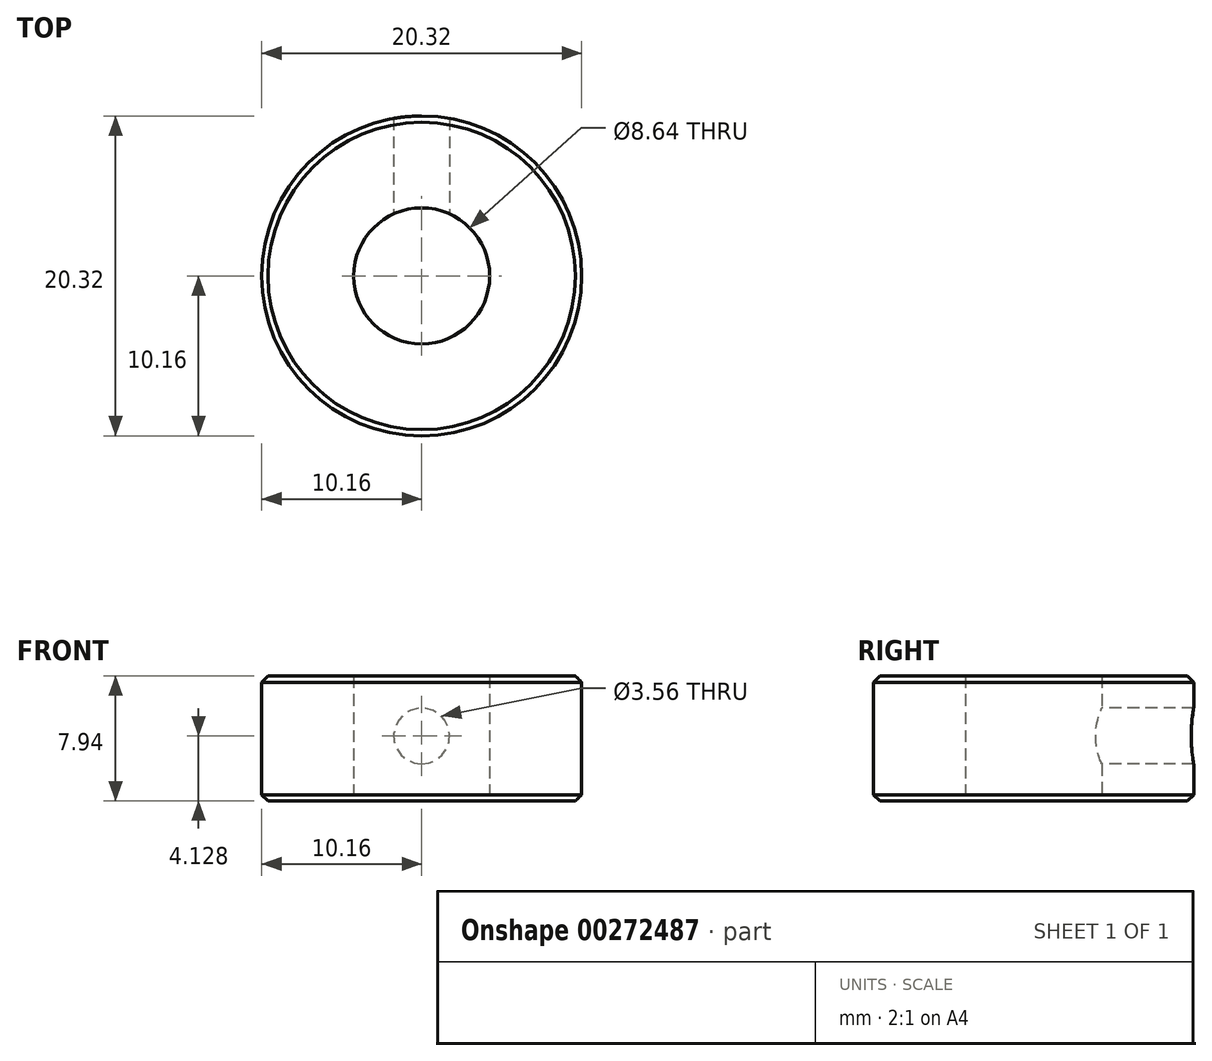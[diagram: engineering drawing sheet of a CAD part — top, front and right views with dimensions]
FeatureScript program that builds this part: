
annotation { "Feature Type Name" : "Feature", "Feature Type Description" : "" }
export const myFeature = defineFeature(function(context is Context, id is Id, definition is map)
    precondition{}
    {
        {
            var Q0;
            Q0=qCreatedBy(makeId("Top.planeOp"),FACE);
            var sketch = newSketch(context, id + "F0", { "sketchPlane" : qUnion([Q0])});
            skCircle(sketch, "E0", {"center": v(0, 0) * mm, "radius": 10.16 * mm});
            skCircle(sketch, "E1", {"center": v(0, 0) * mm, "radius": 4.32 * mm});
            skSolve(sketch);
        }
        {
            var Q0;
            Q0 = qSketchRegion(id + "F0", true);
            extrude(context, id + "F1", {"entities" : qUnion([Q0]), "depth" : 7.94 * mm});
        }
        {
            var Q0;
            Q0=qCreatedBy(makeId("Front.planeOp"),FACE);
            var sketch = newSketch(context, id + "F2", { "sketchPlane" : qUnion([Q0])});
            skCircle(sketch, "E2", {"center": v(0, 4.13) * mm, "radius": 1.78 * mm});
            skSolve(sketch);
        }
        {
            var Q0;
            Q0 = qSketchRegion(id + "F2", true);
            extrude(context, id + "F3", {"entities" : qUnion([Q0]), "operationType" : NewBodyOperationType.REMOVE, "oppositeDirection" : true, "depth" : 25.4 * mm});
        }
        {
            var Q0;
            Q0=makeQuery(id+"F1.opExtrude","CAP_EDGE",EDGE,{"disambiguationData":[OSD([sQuery(id+"F0.wireOp",EDGE,"E0")])],"isStart":true});
            var Q1;
            Q1=makeQuery(id+"F1.opExtrude","CAP_EDGE",EDGE,{"disambiguationData":[OSD([sQuery(id+"F0.wireOp",EDGE,"E0")])],"isStart":false});
            chamfer(context, id + "F4", {"entities" : qUnion([Q0, Q1]), "width" : .4 * mm, "tangentPropagation" : true});
        }
    });
